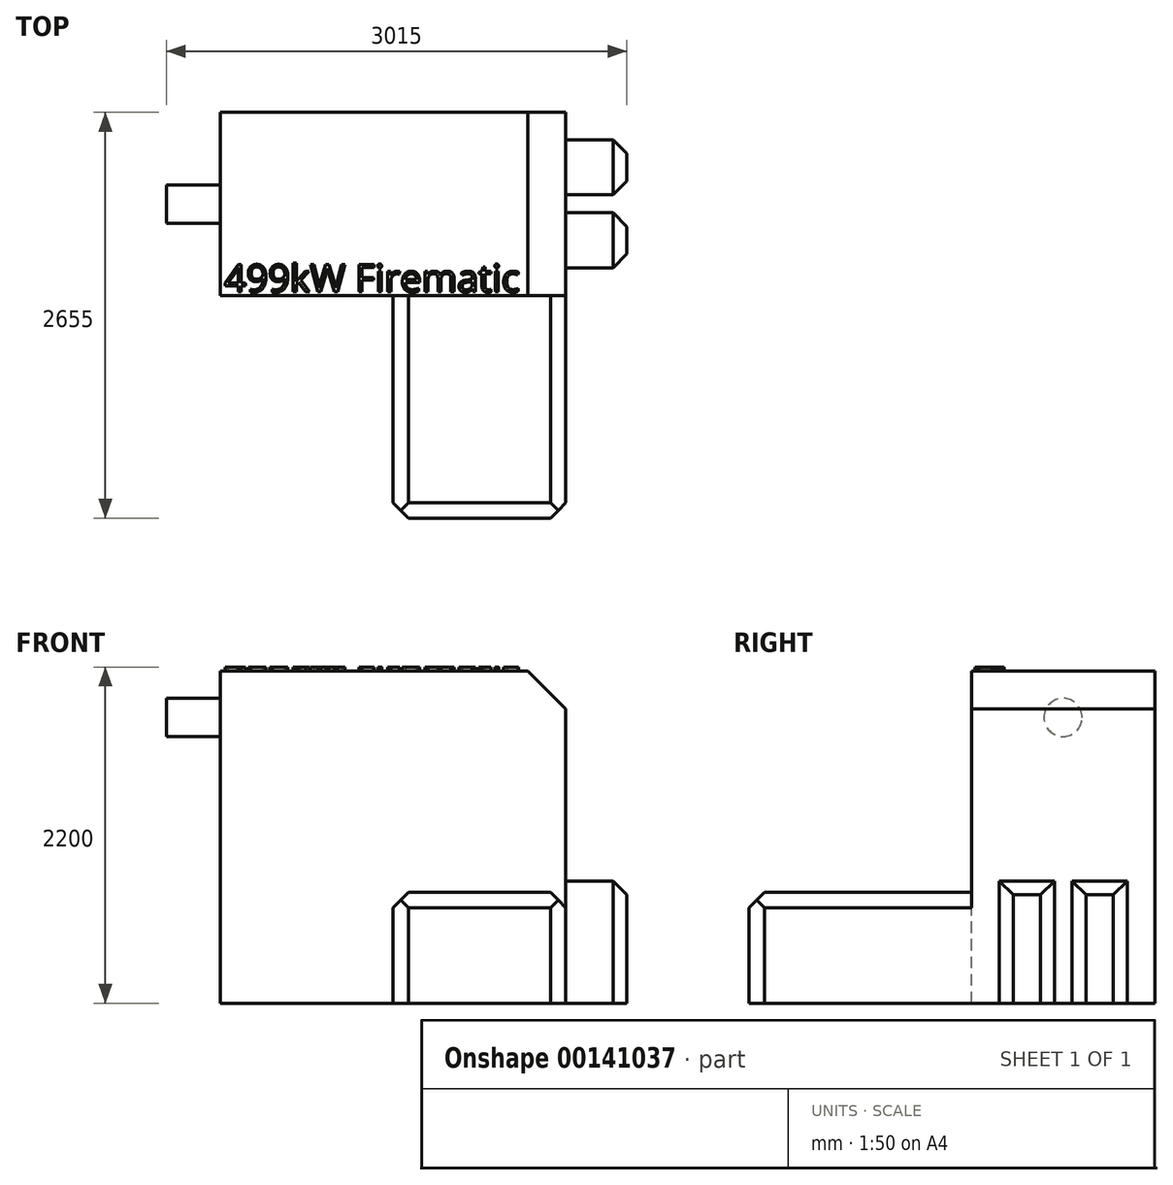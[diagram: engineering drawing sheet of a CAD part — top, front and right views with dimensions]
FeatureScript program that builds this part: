
annotation { "Feature Type Name" : "Feature", "Feature Type Description" : "" }
export const myFeature = defineFeature(function(context is Context, id is Id, definition is map)
    precondition{}
    {
        {
            var Q0;
            Q0=qCreatedBy(makeId("Top.planeOp"),FACE);
            var sketch = newSketch(context, id + "F0", { "sketchPlane" : qUnion([Q0])});
            skLineSegment(sketch, "E0.bottom", {"start": v(0, 0) * mm, "end": v(2260, 0) * mm});
            skLineSegment(sketch, "E0.top", {"start": v(0, 1200) * mm, "end": v(2260, 1200) * mm});
            skLineSegment(sketch, "E0.left", {"start": v(0, 0) * mm, "end": v(0, 1200) * mm});
            skLineSegment(sketch, "E0.right", {"start": v(2260, 0) * mm, "end": v(2260, 1200) * mm});
            skSolve(sketch);
        }
        {
            var Q0;
            Q0=qSketchRegion(id+"F0",true);
            extrude(context, id + "F1", {"entities" : qUnion([Q0]), "depth" : 2175 * mm});
        }
        {
            var Q0;
            Q0=makeQuery(id+"F1.opExtrude","CAP_FACE",FACE,{"disambiguationData":[OSD([sQuery(id+"F0.wireOp",EDGE,"E0.bottom"),sQuery(id+"F0.wireOp",EDGE,"E0.top"),sQuery(id+"F0.wireOp",EDGE,"E0.left"),sQuery(id+"F0.wireOp",EDGE,"E0.right")])],"isStart":false});
            var sketch = newSketch(context, id + "F2", { "sketchPlane" : qUnion([Q0])});
            skText(sketch, "E1", { "text": "499kW Firematic", "fontName": "OpenSans-Regular.ttf"});
            const initialGuessF2  = {"E1": [0.025, 0.025, 1, 0, 0.18]};
            skSetInitialGuess(sketch, initialGuessF2);
            skSolve(sketch);
        }
        {
            var Q0;
            Q0=qSketchRegion(id+"F2",true);
            extrude(context, id + "F3", {"entities" : qUnion([Q0]), "operationType" : NewBodyOperationType.ADD, "depth" : 25 * mm});
        }
        {
            var Q0;
            Q0=makeQuery(id+"F1.opExtrude","SWEPT_FACE",FACE,{"disambiguationData":[OSD([sQuery(id+"F0.wireOp",EDGE,"E0.bottom")])]});
            var sketch = newSketch(context, id + "F4", { "sketchPlane" : qUnion([Q0])});
            skLineSegment(sketch, "E2.bottom", {"start": v(1130, 0) * mm, "end": v(2260, 0) * mm});
            skLineSegment(sketch, "E2.top", {"start": v(1130, 725) * mm, "end": v(2260, 725) * mm});
            skLineSegment(sketch, "E2.left", {"start": v(1130, 0) * mm, "end": v(1130, 725) * mm});
            skLineSegment(sketch, "E2.right", {"start": v(2260, 0) * mm, "end": v(2260, 725) * mm});
            skSolve(sketch);
        }
        {
            var Q0;
            Q0=qSketchRegion(id+"F4",true);
            extrude(context, id + "F5", {"entities" : qUnion([Q0]), "operationType" : NewBodyOperationType.ADD, "depth" : 1455 * mm});
        }
        {
            var Q0;
            Q0=makeQuery(id+"F5.opExtrude","SWEPT_EDGE",EDGE,{"disambiguationData":[OSD([sQuery(id+"F4.wireOp",EDGE,"E2.top"),sQuery(id+"F4.wireOp",EDGE,"E2.left")])]});
            var Q1;
            Q1=makeQuery(id+"F5.opExtrude","SWEPT_EDGE",EDGE,{"disambiguationData":[OSD([sQuery(id+"F0.wireOp",EDGE,"E0.bottom"),sQuery(id+"F0.wireOp",EDGE,"E0.right"),sQuery(id+"F4.wireOp",EDGE,"E2.top"),sQuery(id+"F4.wireOp",EDGE,"E2.right")])]});
            chamfer(context, id + "F6", {"entities" : qUnion([Q0, Q1]), "width" : 100 * mm, "tangentPropagation" : true});
        }
        {
            var Q0;
            Q0=makeQuery(id+"F5.opExtrude","CAP_EDGE",EDGE,{"disambiguationData":[OSD([sQuery(id+"F4.wireOp",EDGE,"E2.top")])],"isStart":false});
            var Q1;
            Q1=makeQuery(id+"F5.opExtrude","CAP_EDGE",EDGE,{"disambiguationData":[OSD([sQuery(id+"F4.wireOp",EDGE,"E2.right")])],"isStart":false});
            var Q2;
            Q2=makeQuery(id+"F5.opExtrude","CAP_EDGE",EDGE,{"disambiguationData":[OSD([sQuery(id+"F4.wireOp",EDGE,"E2.left")])],"isStart":false});
            chamfer(context, id + "F7", {"entities" : qUnion([Q0, Q1, Q2]), "width" : 100 * mm, "tangentPropagation" : true});
        }
        {
            var Q0;
            Q0=makeQuery(id+"F5.boolean.opBoolean","MERGE",FACE,{"derivedFrom":[makeQuery(id+"F1.opExtrude","SWEPT_FACE",FACE,{"disambiguationData":[OSD([sQuery(id+"F0.wireOp",EDGE,"E0.right")])]}),makeQuery(id+"F5.opExtrude","SWEPT_FACE",FACE,{"disambiguationData":[OSD([sQuery(id+"F4.wireOp",EDGE,"E2.right")])]})]});
            var sketch = newSketch(context, id + "F8", { "sketchPlane" : qUnion([Q0])});
            skLineSegment(sketch, "E3.bottom", {"start": v(183, 0) * mm, "end": v(543, 0) * mm});
            skLineSegment(sketch, "E3.top", {"start": v(183, 800) * mm, "end": v(543, 800) * mm});
            skLineSegment(sketch, "E3.left", {"start": v(183, 0) * mm, "end": v(183, 800) * mm});
            skLineSegment(sketch, "E3.right", {"start": v(543, 0) * mm, "end": v(543, 800) * mm});
            skSolve(sketch);
        }
        {
            var Q0;
            Q0=qSketchRegion(id+"F8",true);
            extrude(context, id + "F9", {"entities" : qUnion([Q0]), "operationType" : NewBodyOperationType.ADD, "depth" : 400 * mm});
        }
        {
            var Q0;
            Q0=makeQuery(id+"F9.opExtrude","CAP_EDGE",EDGE,{"disambiguationData":[OSD([sQuery(id+"F8.wireOp",EDGE,"E3.left")])],"isStart":false});
            var Q1;
            Q1=makeQuery(id+"F9.opExtrude","CAP_EDGE",EDGE,{"disambiguationData":[OSD([sQuery(id+"F8.wireOp",EDGE,"E3.top")])],"isStart":false});
            var Q2;
            Q2=makeQuery(id+"F9.opExtrude","CAP_EDGE",EDGE,{"disambiguationData":[OSD([sQuery(id+"F8.wireOp",EDGE,"E3.right")])],"isStart":false});
            chamfer(context, id + "F10", {"entities" : qUnion([Q0, Q1, Q2]), "width" : 90 * mm, "tangentPropagation" : true});
        }
        {
            var Q0;
            Q0=makeQuery(id+"F5.boolean.opBoolean","MERGE",FACE,{"derivedFrom":[makeQuery(id+"F1.opExtrude","SWEPT_FACE",FACE,{"disambiguationData":[OSD([sQuery(id+"F0.wireOp",EDGE,"E0.right")])]}),makeQuery(id+"F5.opExtrude","SWEPT_FACE",FACE,{"disambiguationData":[OSD([sQuery(id+"F4.wireOp",EDGE,"E2.right")])]})]});
            var sketch = newSketch(context, id + "F11", { "sketchPlane" : qUnion([Q0])});
            skLineSegment(sketch, "E4.bottom", {"start": v(660, 0) * mm, "end": v(1020, 0) * mm});
            skLineSegment(sketch, "E4.top", {"start": v(660, 800) * mm, "end": v(1020, 800) * mm});
            skLineSegment(sketch, "E4.left", {"start": v(660, 0) * mm, "end": v(660, 800) * mm});
            skLineSegment(sketch, "E4.right", {"start": v(1020, 0) * mm, "end": v(1020, 800) * mm});
            skSolve(sketch);
        }
        {
            var Q0;
            Q0=qSketchRegion(id+"F11",true);
            var Q1;
            Q1=makeQuery(id+"F9.opExtrude","CAP_FACE",FACE,{"disambiguationData":[OSD([sQuery(id+"F8.wireOp",EDGE,"E3.bottom"),sQuery(id+"F8.wireOp",EDGE,"E3.top"),sQuery(id+"F8.wireOp",EDGE,"E3.left"),sQuery(id+"F8.wireOp",EDGE,"E3.right")])],"isStart":false});
            extrude(context, id + "F12", {"entities" : qUnion([Q0]), "operationType" : NewBodyOperationType.ADD, "endBound" : BoundingType.UP_TO_SURFACE, "endBoundEntityFace" : qUnion([Q1]), "depth" : 25 * mm});
        }
        {
            var Q0;
            Q0=makeQuery(id+"F12.opExtrude","CAP_EDGE",EDGE,{"disambiguationData":[OSD([sQuery(id+"F11.wireOp",EDGE,"E4.right")])],"isStart":false});
            var Q1;
            Q1=makeQuery(id+"F12.opExtrude","CAP_EDGE",EDGE,{"disambiguationData":[OSD([sQuery(id+"F11.wireOp",EDGE,"E4.top")])],"isStart":false});
            var Q2;
            Q2=makeQuery(id+"F12.opExtrude","CAP_EDGE",EDGE,{"disambiguationData":[OSD([sQuery(id+"F11.wireOp",EDGE,"E4.left")])],"isStart":false});
            chamfer(context, id + "F13", {"entities" : qUnion([Q0, Q1, Q2]), "width" : 90 * mm, "tangentPropagation" : true});
        }
        {
            var Q0;
            Q0=makeQuery(id+"F1.opExtrude","SWEPT_FACE",FACE,{"disambiguationData":[OSD([sQuery(id+"F0.wireOp",EDGE,"E0.left")])]});
            var sketch = newSketch(context, id + "F14", { "sketchPlane" : qUnion([Q0])});
            skCircle(sketch, "E5", {"center": v(-600, 1870) * mm, "radius": 125 * mm});
            skSolve(sketch);
        }
        {
            var Q0;
            Q0=qSketchRegion(id+"F14",true);
            extrude(context, id + "F15", {"entities" : qUnion([Q0]), "operationType" : NewBodyOperationType.ADD, "depth" : 355 * mm});
        }
        {
            var Q0;
            Q0=makeQuery(id+"F1.opExtrude","CAP_EDGE",EDGE,{"disambiguationData":[OSD([sQuery(id+"F0.wireOp",EDGE,"E0.right")])],"isStart":false});
            chamfer(context, id + "F16", {"entities" : qUnion([Q0]), "width" : 250 * mm, "tangentPropagation" : true});
        }
    });
